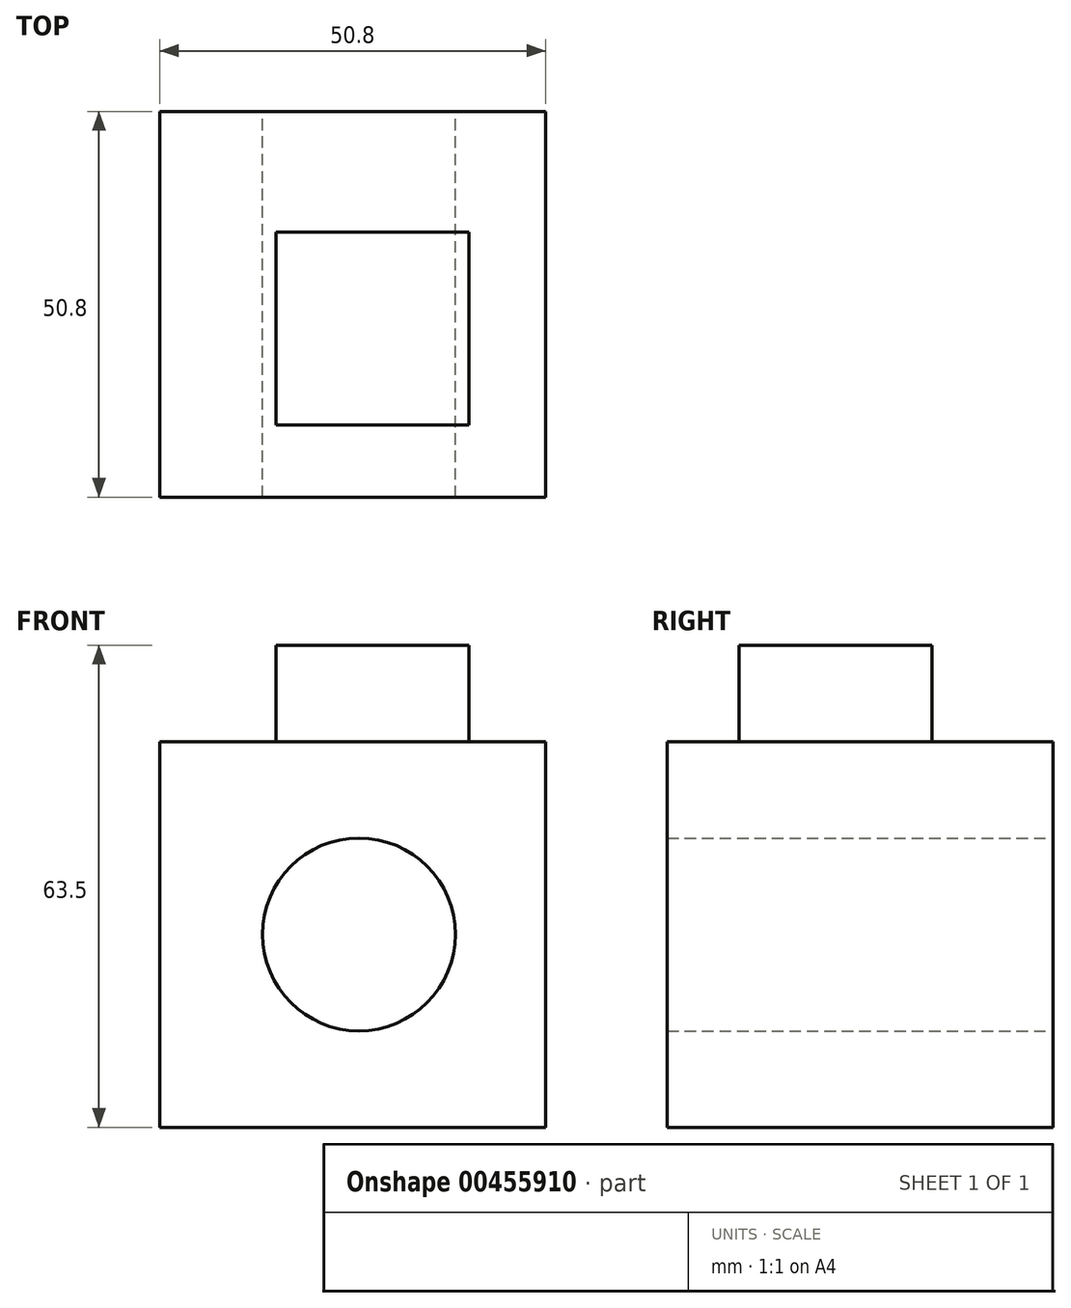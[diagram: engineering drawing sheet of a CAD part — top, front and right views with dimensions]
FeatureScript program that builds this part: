
annotation { "Feature Type Name" : "Feature", "Feature Type Description" : "" }
export const myFeature = defineFeature(function(context is Context, id is Id, definition is map)
    precondition{}
    {
        {
            var Q0;
            Q0=qCreatedBy(makeId("Front.planeOp"),FACE);
            var sketch = newSketch(context, id + "F0", { "sketchPlane" : qUnion([Q0])});
            skLineSegment(sketch, "E0.bottom", {"start": v(-35.86, 30.92) * mm, "end": v(14.94, 30.92) * mm});
            skLineSegment(sketch, "E0.top", {"start": v(-35.86, -19.88) * mm, "end": v(14.94, -19.88) * mm});
            skLineSegment(sketch, "E0.left", {"start": v(-35.86, 30.92) * mm, "end": v(-35.86, -19.88) * mm});
            skLineSegment(sketch, "E0.right", {"start": v(14.94, 30.92) * mm, "end": v(14.94, -19.88) * mm});
            skCircle(sketch, "E1", {"center": v(-9.64, 5.52) * mm, "radius": 12.7 * mm});
            skSolve(sketch);
        }
        {
            var Q0;
            Q0=makeQuery(id+"F0.imprint","IMPRINT",FACE,{"disambiguationData":[TD([[makeQuery(id+"F0.imprint","IMPRINT",EDGE,{"derivedFrom":sQuery(id+"F0.wireOp",EDGE,"E0.bottom")}),-1.0]])]});
            extrude(context, id + "F1", {"entities" : qUnion([Q0]), "depth" : 50.8 * mm});
        }
        {
            var Q0;
            Q0=makeQuery(id+"F1.opExtrude","SWEPT_FACE",FACE,{"disambiguationData":[OSD([sQuery(id+"F0.wireOp",EDGE,"E0.bottom")])]});
            var sketch = newSketch(context, id + "F2", { "sketchPlane" : qUnion([Q0])});
            skLineSegment(sketch, "E2.bottom", {"start": v(-20.58, -15.93) * mm, "end": v(4.82, -15.93) * mm});
            skLineSegment(sketch, "E2.top", {"start": v(-20.58, -41.33) * mm, "end": v(4.82, -41.33) * mm});
            skLineSegment(sketch, "E2.left", {"start": v(-20.58, -15.93) * mm, "end": v(-20.58, -41.33) * mm});
            skLineSegment(sketch, "E2.right", {"start": v(4.82, -15.93) * mm, "end": v(4.82, -41.33) * mm});
            skSolve(sketch);
        }
        {
            var Q0;
            Q0 = qSketchRegion(id + "F2", true);
            extrude(context, id + "F3", {"entities" : qUnion([Q0]), "operationType" : NewBodyOperationType.ADD, "depth" : 12.7 * mm});
        }
    });
